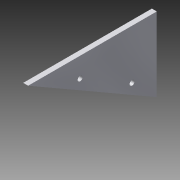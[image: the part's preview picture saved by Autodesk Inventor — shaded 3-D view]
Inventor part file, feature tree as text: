
AUTODESK INVENTOR PART (.ipt)
format: ipt  version: 2015 SP1 (Build 190203100, 203)  size: 99,328 bytes
history: native  units: in
note: dims shown in document units (in); Inventor stores cm internally (conversion verified against a paired STEP export)
features: sketch x2, extrude x1, hole x1
ambient origin geometry x8: Origin, YZ Plane, XZ Plane, XY Plane, X Axis, Y Axis, Z Axis, Center Point
bodies: Solid1 (feature_tree)
feature tree (4):
  extrude  "Extrusion1"  Depth=3.75in
  hole  "Hole1"  [1 undecoded]
  sketch  "Sketch1"  dims[d0=6.5in d1=3.75in]
  sketch  "Sketch2"  dims[d2=0.25in d3=0.0in d4=1.0in d5=3.875in d6=1.25in d7=2.5in d8=0.25in d9=0.75in d10=0.375in d11=0.25in d12=0.5635in d13=1.0in d14=0.8108in]
note: 1 required parameter value undecoded (feature->parameter linkage not recoverable at this tier; creation-order binding heuristic only, values carry confidence <= 0.55)
